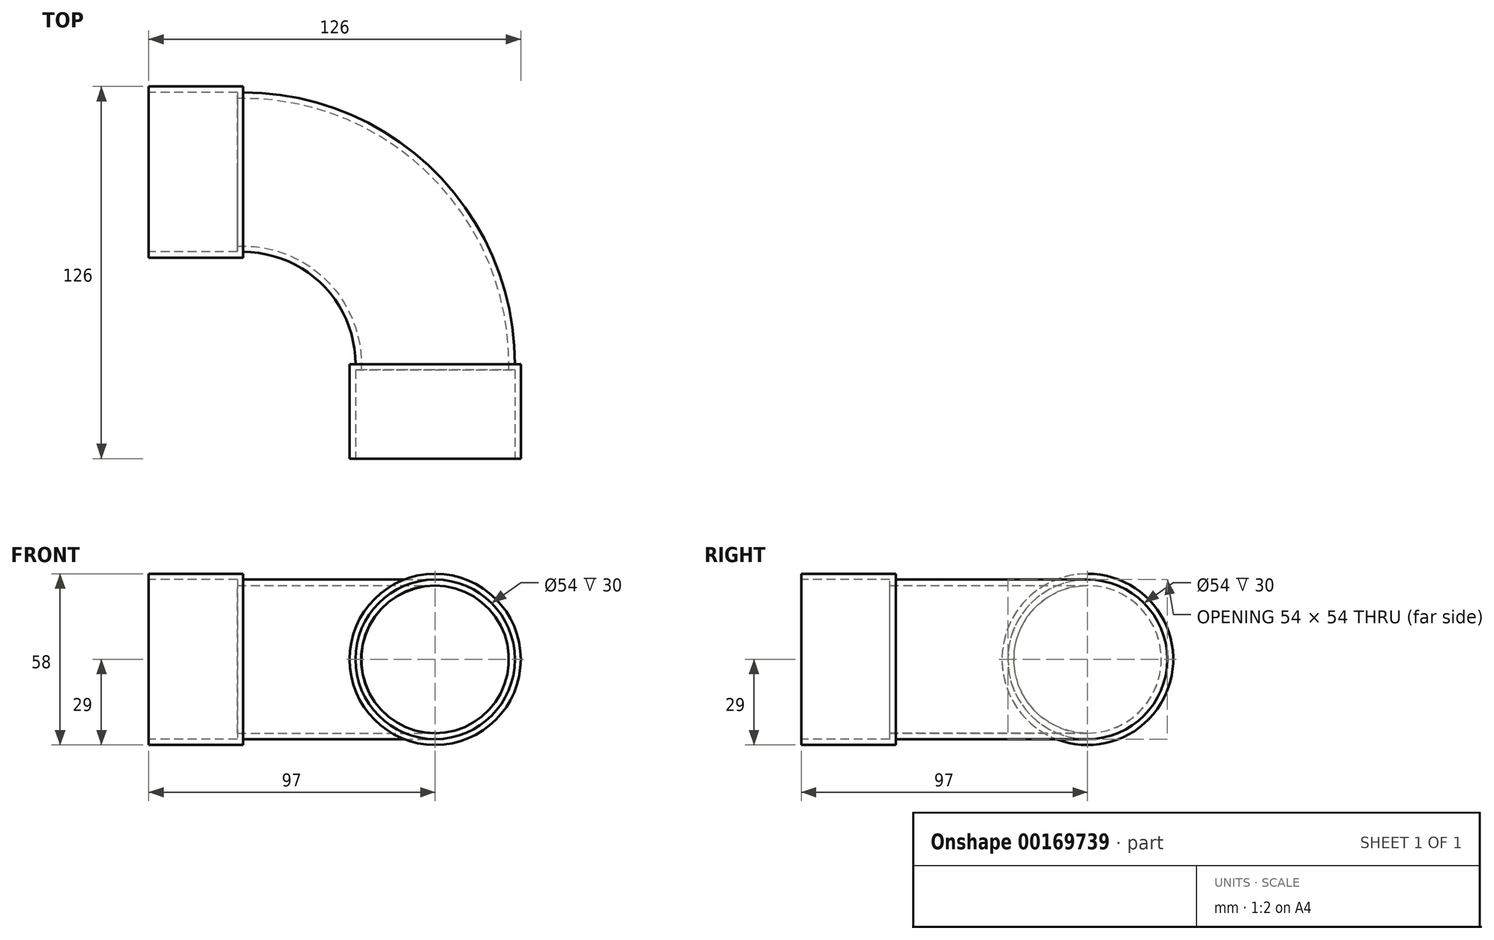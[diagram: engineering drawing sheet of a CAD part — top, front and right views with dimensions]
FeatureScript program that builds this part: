
annotation { "Feature Type Name" : "Feature", "Feature Type Description" : "" }
export const myFeature = defineFeature(function(context is Context, id is Id, definition is map)
    precondition{}
    {
        {
            var Q0;
            Q0=qCreatedBy(makeId("Top.planeOp"),FACE);
            var sketch = newSketch(context, id + "F0", { "sketchPlane" : qUnion([Q0])});
            skArc(sketch, "E0", {"start": v(65, 0) * mm, "mid": v(45.96, 45.96) * mm, "end": v(0, 65) * mm});
            skLineSegment(sketch, "E1", {"start": v(0, 65) * mm, "end": v(-32, 65) * mm});
            skLineSegment(sketch, "E2", {"start": v(65, 0) * mm, "end": v(65, -32) * mm});
            skSolve(sketch);
        }
        {
            var Q0;
            Q0=sQuery(id+"F0.wireOp",VERTEX,"E1.end");
            var Q1;
            Q1=qCreatedBy(makeId("Right.planeOp"),FACE);
            cPlane(context, id + "F1", {"entities" : qUnion([Q0, Q1]), "cplaneType" : CPlaneType.PLANE_POINT, "offset" : 25 * mm, "width" : 150 * mm, "height" : 150 * mm});
        }
        {
            var Q0;
            Q0=qCreatedBy(id+"F1.planeOp",FACE);
            var sketch = newSketch(context, id + "F2", { "sketchPlane" : qUnion([Q0])});
            skPoint(sketch, "E3.0", {"position": v(65, 0) * mm});
            skCircle(sketch, "E4", {"center": v(65, 0) * mm, "radius": 27 * mm});
            skSolve(sketch);
        }
        {
            var Q0;
            Q0=makeQuery(id+"F2.imprint","IMPRINT",FACE,{"disambiguationData":[TD([[makeQuery(id+"F2.imprint","IMPRINT",EDGE,{"derivedFrom":sQuery(id+"F2.wireOp",EDGE,"E4")}),1.0]])]});
            var Q1;
            Q1=sQuery(id+"F0.wireOp",EDGE,"E1");
            var Q2;
            Q2=sQuery(id+"F0.wireOp",EDGE,"E0");
            var Q3;
            Q3=sQuery(id+"F0.wireOp",EDGE,"E2");
            sweep(context, id + "F3", {"profiles" : qUnion([Q0]), "path" : qUnion([Q1, Q2, Q3])});
        }
        {
            var Q0;
            Q0=makeQuery(id+"F3.opSweep","CAP_FACE",FACE,{"disambiguationData":[OSD([sQuery(id+"F0.wireOp",VERTEX,"E1.end"),sQuery(id+"F2.wireOp",EDGE,"E4")])],"isStart":true});
            var sketch = newSketch(context, id + "F4", { "sketchPlane" : qUnion([Q0])});
            skCircle(sketch, "E5", {"center": v(-65, 0) * mm, "radius": 29 * mm});
            skSolve(sketch);
        }
        {
            var Q0;
            Q0=makeQuery(id+"F4.imprint","IMPRINT",FACE,{"disambiguationData":[TD([[makeQuery(id+"F4.imprint","IMPRINT",EDGE,{"derivedFrom":makeQuery(id+"F3.opSweep","CAP_EDGE",EDGE,{"disambiguationData":[OSD([sQuery(id+"F0.wireOp",VERTEX,"E1.end"),sQuery(id+"F2.wireOp",EDGE,"E4")])],"isStart":true})}),-1.0]])]});
            var Q1;
            Q1=makeQuery(id+"F4.imprint","IMPRINT",FACE,{"disambiguationData":[TD([[makeQuery(id+"F4.imprint","IMPRINT",EDGE,{"derivedFrom":sQuery(id+"F4.wireOp",EDGE,"E5")}),1.0]])]});
            extrude(context, id + "F5", {"entities" : qUnion([Q0, Q1]), "operationType" : NewBodyOperationType.ADD, "oppositeDirection" : true, "depth" : 32 * mm});
        }
        {
            var Q0;
            Q0=makeQuery(id+"F3.opSweep","CAP_FACE",FACE,{"disambiguationData":[OSD([sQuery(id+"F0.wireOp",VERTEX,"E2.end"),sQuery(id+"F2.wireOp",EDGE,"E4")])],"isStart":false});
            var sketch = newSketch(context, id + "F6", { "sketchPlane" : qUnion([Q0])});
            skCircle(sketch, "E6", {"center": v(65, 0) * mm, "radius": 29 * mm});
            skSolve(sketch);
        }
        {
            var Q0;
            Q0=makeQuery(id+"F6.imprint","IMPRINT",FACE,{"disambiguationData":[TD([[makeQuery(id+"F6.imprint","IMPRINT",EDGE,{"derivedFrom":sQuery(id+"F6.wireOp",EDGE,"E6")}),1.0]])]});
            var Q1;
            Q1=makeQuery(id+"F6.imprint","IMPRINT",FACE,{"disambiguationData":[TD([[makeQuery(id+"F6.imprint","IMPRINT",EDGE,{"derivedFrom":makeQuery(id+"F3.opSweep","CAP_EDGE",EDGE,{"disambiguationData":[OSD([sQuery(id+"F0.wireOp",VERTEX,"E2.end"),sQuery(id+"F2.wireOp",EDGE,"E4")])],"isStart":false})}),1.0]])]});
            extrude(context, id + "F7", {"entities" : qUnion([Q0, Q1]), "operationType" : NewBodyOperationType.ADD, "oppositeDirection" : true, "depth" : 32 * mm});
        }
        {
            var Q0;
            Q0=makeQuery(id+"F7.boolean.opBoolean","MERGE",FACE,{"derivedFrom":[makeQuery(id+"F3.opSweep","CAP_FACE",FACE,{"disambiguationData":[OSD([sQuery(id+"F0.wireOp",VERTEX,"E2.end"),sQuery(id+"F2.wireOp",EDGE,"E4")])],"isStart":false}),makeQuery(id+"F7.opExtrude","CAP_FACE",FACE,{"disambiguationData":[OSD([sQuery(id+"F6.wireOp",EDGE,"E6")])],"isStart":true})]});
            var Q1;
            Q1=makeQuery(id+"F5.boolean.opBoolean","MERGE",FACE,{"derivedFrom":[makeQuery(id+"F3.opSweep","CAP_FACE",FACE,{"disambiguationData":[OSD([sQuery(id+"F0.wireOp",VERTEX,"E1.end"),sQuery(id+"F2.wireOp",EDGE,"E4")])],"isStart":true}),makeQuery(id+"F5.opExtrude","CAP_FACE",FACE,{"disambiguationData":[OSD([sQuery(id+"F4.wireOp",EDGE,"E5")])],"isStart":true})]});
            shell(context, id + "F8", {"entities" : qUnion([Q0, Q1]), "thickness" : 2 * mm});
        }
    });
